# Revit family: Скамейка стальная «Пифагор» без спинки Арт 11129
name_source: partatom
category: Антураж
revit_build: Autodesk Revit 2018 (Build: 20180423_1000(x64)
units: mm (PartAtom-declared; Revit-internal decimal feet)

## family parameters
Всегда вертикально = Да
Источник визуального образа = Геометрия семейства
На основе рабочей плоскости = Нет
Общий = Нет
При загрузке вырезать с полостями = Нет
Точка расчета площади = Нет

## types (12) — shared parameters
URL = https://hobbyka.ru
Артикул товара = Арт. 10895
Высота = 451 мм
Группа модели = Скамейки
Изготовитель = ООО «Хоббика»
Описание = Сталь, дерево
Цвет опоры = Сталь
Цвет отделки = Дерево
Ширина = 653 мм

## per-type parameters (varying)
| type | Версия 1,2 м | Версия 1,5 м | Версия 1,8 м | Версия 2,0 м | Версия 2,5 м | Версия 3,0 м | Версия 3,5 м | Версия 4,0 м | Версия 4,5 м | Версия 5,0 м | Версия 5,5 м | Версия 6,0 м | Длина | Изображение типоразмера | Материал изделия | Средняя опора |
| Версия 1,2 м | Да | Нет | Нет | Нет | Нет | Нет | Нет | Нет | Нет | Нет | Нет | Нет | 1200 мм | Скамейка стальная «Пифагор» без спинки Арт 11129.jpg | Скамейка стальная «Пифагор» без спинки. Версия 1,2 м | Нет |
| Версия 1,5 м | Нет | Да | Нет | Нет | Нет | Нет | Нет | Нет | Нет | Нет | Нет | Нет | 1500 мм | Скамейка стальная «Пифагор» без спинки Арт 11129.jpg | Скамейка стальная «Пифагор» без спинки. Версия 1,5 м | Нет |
| Версия 1,8 м | Нет | Нет | Да | Нет | Нет | Нет | Нет | Нет | Нет | Нет | Нет | Нет | 1800 мм | Скамейка стальная «Пифагор» без спинки Арт 11129.jpg | Скамейка стальная «Пифагор» без спинки. Версия 1,8 м | Нет |
| Версия 2,0 м | Нет | Нет | Нет | Да | Нет | Нет | Нет | Нет | Нет | Нет | Нет | Нет | 2000 мм | Скамейка стальная «Пифагор» без спинки Арт 11129.jpg | Скамейка стальная «Пифагор» без спинки. Версия 2,0 м | Нет |
| Версия 2,5 м | Нет | Нет | Нет | Нет | Да | Нет | Нет | Нет | Нет | Нет | Нет | Нет | 2500 мм | Скамейка стальная «Пифагор» без спинки Арт 11129.jpg | Скамейка стальная «Пифагор» без спинки. Версия 2,5 м | Нет |
| Версия 3,0 м | Нет | Нет | Нет | Нет | Нет | Да | Нет | Нет | Нет | Нет | Нет | Нет | 3000 мм | Скамейка стальная «Пифагор» без спинки Арт 11129 три опоры.jpg | Скамейка стальная «Пифагор» без спинки. Версия 3,0 м | Да |
| Версия 3,5 м | Нет | Нет | Нет | Нет | Нет | Нет | Да | Нет | Нет | Нет | Нет | Нет | 3500 мм | Скамейка стальная «Пифагор» без спинки Арт 11129 три опоры.jpg | Скамейка стальная «Пифагор» без спинки. Версия 3,5 м | Да |
| Версия 4,0 м | Нет | Нет | Нет | Нет | Нет | Нет | Нет | Да | Нет | Нет | Нет | Нет | 4000 мм | Скамейка стальная «Пифагор» без спинки Арт 11129 три опоры.jpg | Скамейка стальная «Пифагор» без спинки. Версия 4,0 м | Да |
| Версия 4,5 м | Нет | Нет | Нет | Нет | Нет | Нет | Нет | Нет | Да | Нет | Нет | Нет | 4500 мм | Скамейка стальная «Пифагор» без спинки Арт 11129 три опоры.jpg | Скамейка стальная «Пифагор» без спинки. Версия 4,5 м | Да |
| Версия 5,0 м | Нет | Нет | Нет | Нет | Нет | Нет | Нет | Нет | Нет | Да | Нет | Нет | 5000 мм | Скамейка стальная «Пифагор» без спинки Арт 11129 три опоры.jpg | Скамейка стальная «Пифагор» без спинки. Версия 5,0 м | Да |
| Версия 5,5 м | Нет | Нет | Нет | Нет | Нет | Нет | Нет | Нет | Нет | Нет | Да | Нет | 5500 мм | Скамейка стальная «Пифагор» без спинки Арт 11129 три опоры.jpg | Скамейка стальная «Пифагор» без спинки. Версия 5,5 м | Да |
| Версия 6,0 м | Нет | Нет | Нет | Нет | Нет | Нет | Нет | Нет | Нет | Нет | Нет | Да | 6000 мм | Скамейка стальная «Пифагор» без спинки Арт 11129 три опоры.jpg | Скамейка стальная «Пифагор» без спинки. Версия 6,0 м | Да |
